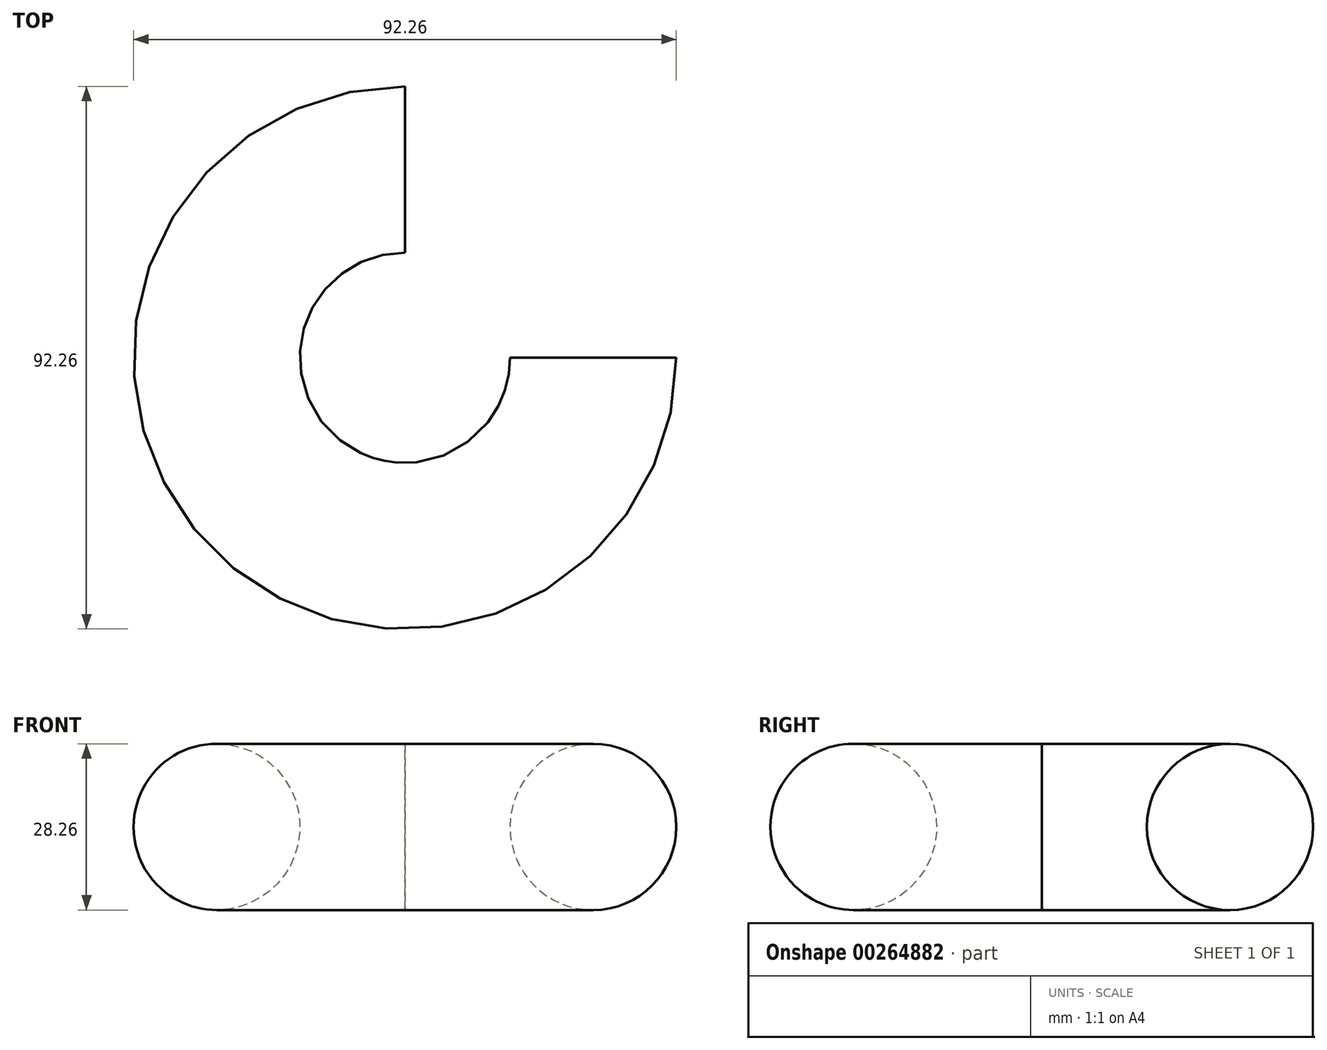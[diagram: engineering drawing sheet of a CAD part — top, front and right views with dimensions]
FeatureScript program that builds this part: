
annotation { "Feature Type Name" : "Feature", "Feature Type Description" : "" }
export const myFeature = defineFeature(function(context is Context, id is Id, definition is map)
    precondition{}
    {
        {
            var Q0;
            Q0=qCreatedBy(makeId("Front.planeOp"),FACE);
            var sketch = newSketch(context, id + "F0", { "sketchPlane" : qUnion([Q0])});
            skCircle(sketch, "E0", {"center": v(32, 0) * mm, "radius": 14.13 * mm});
            skLineSegment(sketch, "E1", {"start": v(0, 32.25) * mm, "end": v(0, -49.79) * mm, "construction": true});
            skSolve(sketch);
        }
        {
            var Q0;
            Q0=sQuery(id+"F0.wireOp",EDGE,"E1");
            var Q1;
            Q1=sQuery(id+"F0.wireOp",EDGE,"E0");
            var Q2;
            Q2=sQuery(id+"F0.wireOp",EDGE,"E1");
            revolve(context, id + "F1", {"bodyType" : ToolBodyType.SURFACE, "surfaceEntities" : qUnion([Q0, Q1]), "axis" : qUnion([Q2]), "revolveType" : RevolveType.ONE_DIRECTION, "angle" : 270 * degree});
        }
    });
